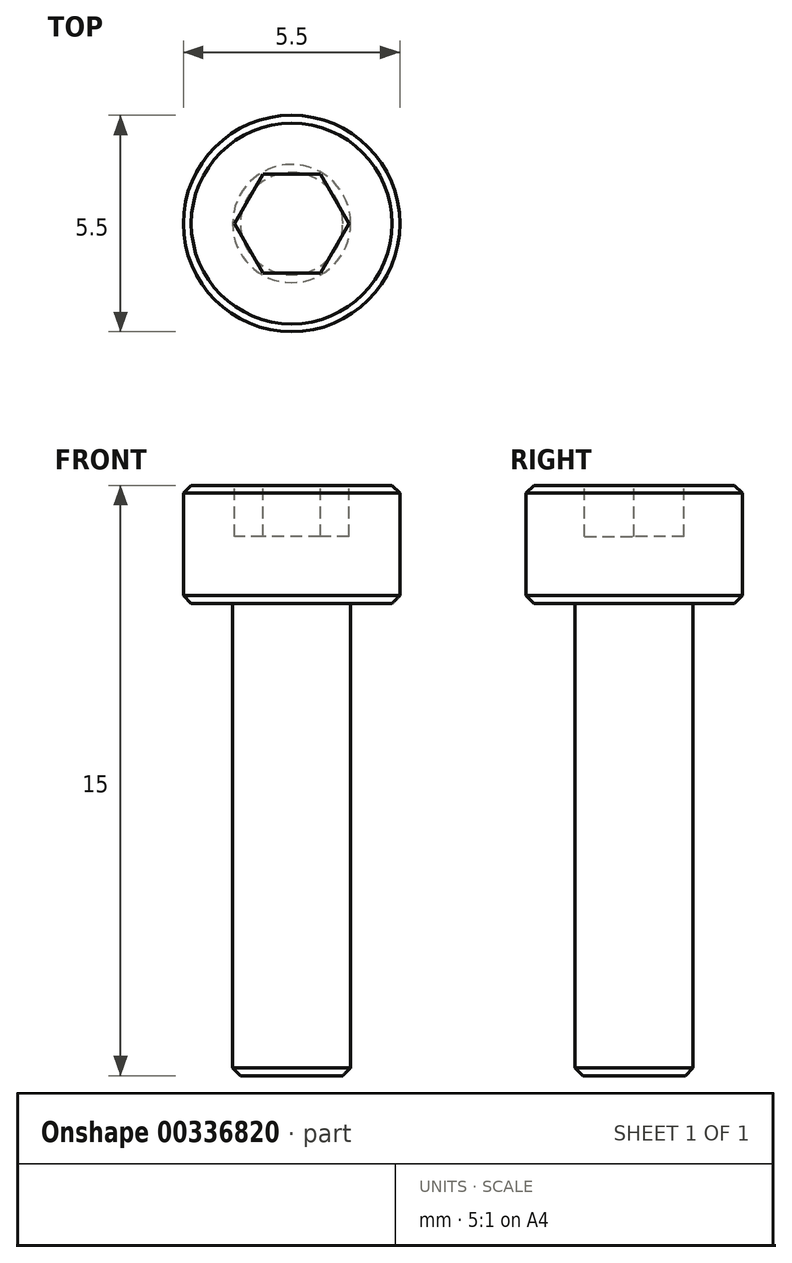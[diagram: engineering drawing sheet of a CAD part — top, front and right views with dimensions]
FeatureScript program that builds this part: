
annotation { "Feature Type Name" : "Feature", "Feature Type Description" : "" }
export const myFeature = defineFeature(function(context is Context, id is Id, definition is map)
    precondition{}
    {
        {
            var Q0;
            Q0=qCreatedBy(makeId("Front.planeOp"),FACE);
            var sketch = newSketch(context, id + "F0", { "sketchPlane" : qUnion([Q0])});
            skLineSegment(sketch, "E0", {"start": v(0, 0) * mm, "end": v(0, -15) * mm});
            skLineSegment(sketch, "E1", {"start": v(0, -15) * mm, "end": v(1.5, -15) * mm});
            skLineSegment(sketch, "E2", {"start": v(1.5, -15) * mm, "end": v(1.5, -3) * mm});
            skLineSegment(sketch, "E3", {"start": v(1.5, -3) * mm, "end": v(2.75, -3) * mm});
            skLineSegment(sketch, "E4", {"start": v(2.75, -3) * mm, "end": v(2.75, 0) * mm});
            skLineSegment(sketch, "E5", {"start": v(2.75, 0) * mm, "end": v(0, 0) * mm});
            skLineSegment(sketch, "E6.MirrorCS", {"start": v(-2.75, -3) * mm, "end": v(-2.75, 0) * mm, "construction": true});
            skLineSegment(sketch, "E7.MirrorCS", {"start": v(-1.5, -15) * mm, "end": v(-1.5, -3) * mm, "construction": true});
            skSolve(sketch);
        }
        {
            var Q0;
            Q0 = qSketchRegion(id + "F0", true);
            var Q1;
            Q1=sQuery(id+"F0.wireOp",EDGE,"E0");
            revolve(context, id + "F1", {"entities" : qUnion([Q0]), "axis" : qUnion([Q1]), "revolveType" : RevolveType.FULL});
        }
        {
            var Q0;
            Q0=makeQuery(id+"F1.opRevolve","SWEPT_FACE",FACE,{"disambiguationData":[OSD([sQuery(id+"F0.wireOp",EDGE,"E5")])]});
            var sketch = newSketch(context, id + "F2", { "sketchPlane" : qUnion([Q0])});
            skCircle(sketch, "E8.cCircle", {"center": v(0, 0) * mm, "radius": 1.26 * mm, "construction": true});
            skLineSegment(sketch, "E8.0", {"start": v(-0.73, -1.26) * mm, "end": v(-1.45, 0) * mm});
            skLineSegment(sketch, "E8.1", {"start": v(-1.45, 0) * mm, "end": v(-0.73, 1.26) * mm});
            skLineSegment(sketch, "E8.2", {"start": v(-0.73, 1.26) * mm, "end": v(0.73, 1.26) * mm});
            skLineSegment(sketch, "E8.3", {"start": v(0.73, 1.26) * mm, "end": v(1.45, 0) * mm});
            skLineSegment(sketch, "E8.4", {"start": v(1.45, 0) * mm, "end": v(0.73, -1.26) * mm});
            skLineSegment(sketch, "E8.5", {"start": v(0.73, -1.26) * mm, "end": v(-0.73, -1.26) * mm});
            skPoint(sketch, "E8.0.midPoint", {"position": v(-1.1, -0.63) * mm});
            skSolve(sketch);
        }
        {
            var Q0;
            Q0 = qSketchRegion(id + "F2", true);
            extrude(context, id + "F3", {"entities" : qUnion([Q0]), "operationType" : NewBodyOperationType.REMOVE, "oppositeDirection" : true, "depth" : 1.3 * mm});
        }
        {
            var Q0;
            Q0=makeQuery(id+"F1.opRevolve","SWEPT_FACE",FACE,{"disambiguationData":[OSD([sQuery(id+"F0.wireOp",EDGE,"E4")])]});
            var Q1;
            Q1=makeQuery(id+"F1.opRevolve","SWEPT_EDGE",EDGE,{"disambiguationData":[OSD([sQuery(id+"F0.wireOp",EDGE,"E1"),sQuery(id+"F0.wireOp",EDGE,"E2")])]});
            chamfer(context, id + "F4", {"entities" : qUnion([Q0, Q1]), "width" : 0.2 * mm, "tangentPropagation" : true});
        }
    });
